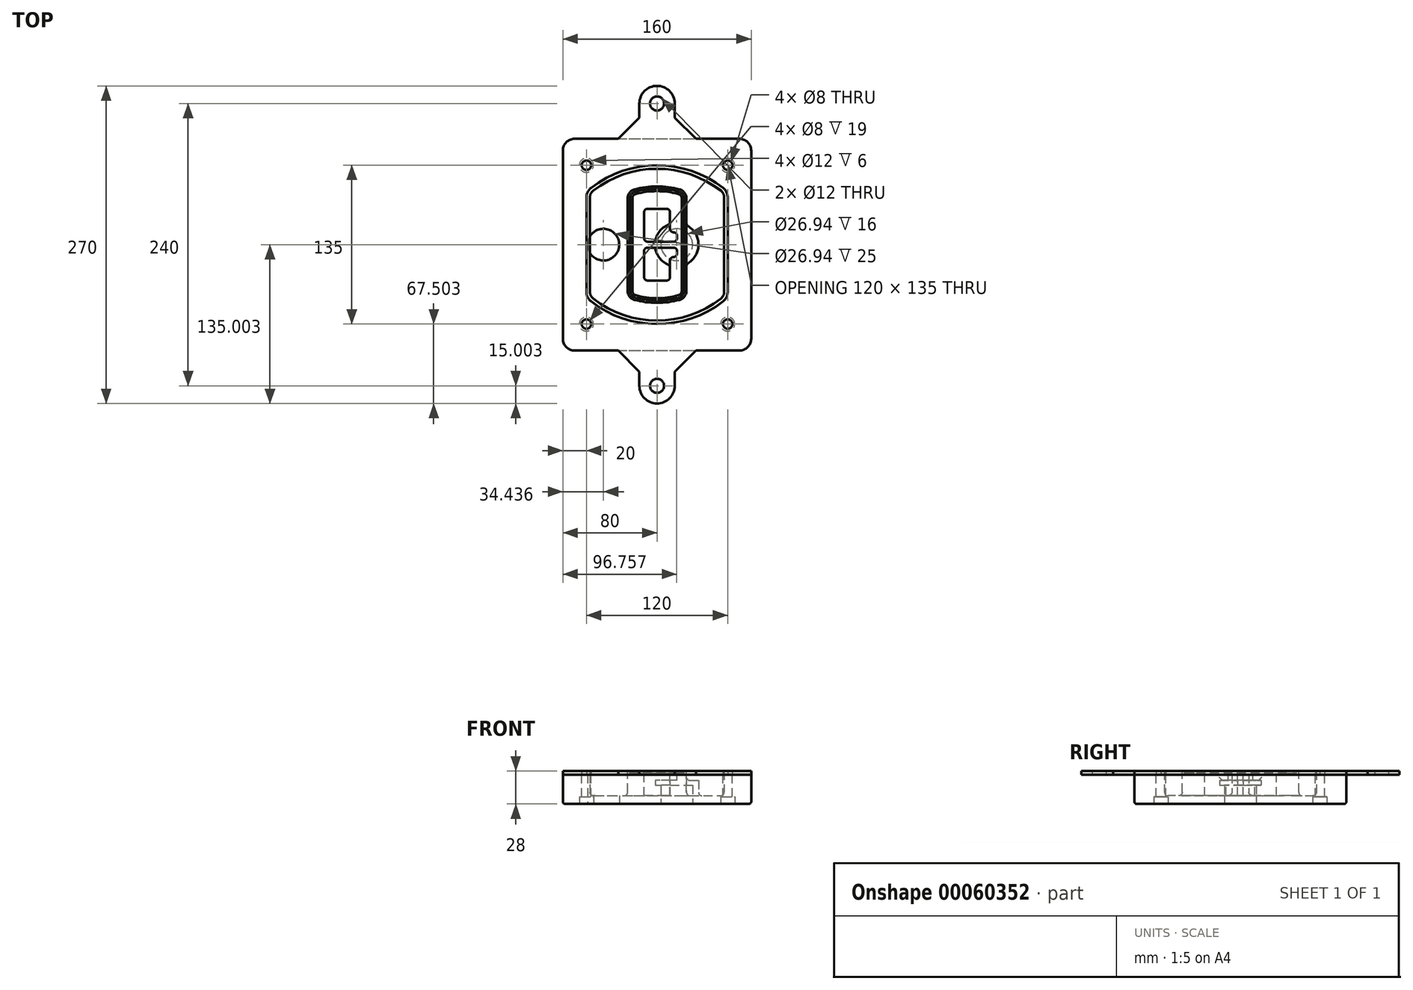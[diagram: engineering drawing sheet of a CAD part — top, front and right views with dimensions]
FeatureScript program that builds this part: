
annotation { "Feature Type Name" : "Feature", "Feature Type Description" : "" }
export const myFeature = defineFeature(function(context is Context, id is Id, definition is map)
    precondition{}
    {
        {
            var Q0;
            Q0=qCreatedBy(makeId("Top.planeOp"),FACE);
            var sketch = newSketch(context, id + "F0", { "sketchPlane" : qUnion([Q0])});
            skPoint(sketch, "E0.rect.middle", {"position": v(0, 0) * mm});
            skLineSegment(sketch, "E1.bottom", {"start": v(24.05, 28.38) * mm, "end": v(164.05, 28.38) * mm});
            skLineSegment(sketch, "E1.top", {"start": v(24.05, 208.38) * mm, "end": v(164.05, 208.38) * mm});
            skLineSegment(sketch, "E1.left", {"start": v(14.05, 38.38) * mm, "end": v(14.05, 198.38) * mm});
            skLineSegment(sketch, "E1.right", {"start": v(174.05, 38.38) * mm, "end": v(174.05, 198.38) * mm});
            skLineSegment(sketch, "E2", {"start": v(14.05, 208.38) * mm, "end": v(174.05, 28.38) * mm, "construction": true});
            skLineSegment(sketch, "E3", {"start": v(174.05, 208.38) * mm, "end": v(14.05, 28.38) * mm, "construction": true});
            skCircle(sketch, "E4", {"center": v(34.05, 185.88) * mm, "radius": 4 * mm});
            skCircle(sketch, "E5", {"center": v(154.05, 185.88) * mm, "radius": 4 * mm});
            skCircle(sketch, "E6", {"center": v(154.05, 50.88) * mm, "radius": 4 * mm});
            skCircle(sketch, "E7", {"center": v(34.05, 50.88) * mm, "radius": 4 * mm});
            skLineSegment(sketch, "E8", {"start": v(34.05, 185.88) * mm, "end": v(154.05, 185.88) * mm, "construction": true});
            skLineSegment(sketch, "E9", {"start": v(154.05, 185.88) * mm, "end": v(154.05, 50.88) * mm, "construction": true});
            skLineSegment(sketch, "E10", {"start": v(154.05, 50.88) * mm, "end": v(34.05, 50.88) * mm, "construction": true});
            skLineSegment(sketch, "E11", {"start": v(34.05, 50.88) * mm, "end": v(34.05, 185.88) * mm, "construction": true});
            skLineSegment(sketch, "E12", {"start": v(34.05, 158.68) * mm, "end": v(34.05, 78.09) * mm});
            skLineSegment(sketch, "E13", {"start": v(154.05, 158.68) * mm, "end": v(154.05, 78.09) * mm});
            skArc(sketch, "E14", {"start": v(150.2, 166.56) * mm, "mid": v(94.05, 185.88) * mm, "end": v(37.9, 166.56) * mm});
            skArc(sketch, "E15", {"start": v(37.9, 70.2) * mm, "mid": v(94.05, 50.88) * mm, "end": v(150.2, 70.2) * mm});
            skLineSegment(sketch, "E16", {"start": v(34.05, 118.38) * mm, "end": v(154.05, 118.38) * mm, "construction": true});
            skPoint(sketch, "E17.visualSharp", {"position": v(34.05, 73.38) * mm});
            skArc(sketch, "E17.filletArc", {"start": v(34.05, 78.09) * mm, "mid": v(35.06, 73.7) * mm, "end": v(37.9, 70.2) * mm});
            skPoint(sketch, "E18.visualSharp", {"position": v(34.05, 163.38) * mm});
            skArc(sketch, "E18.filletArc", {"start": v(37.9, 166.56) * mm, "mid": v(35.06, 163.06) * mm, "end": v(34.05, 158.68) * mm});
            skPoint(sketch, "E19.visualSharp", {"position": v(154.05, 163.38) * mm});
            skArc(sketch, "E19.filletArc", {"start": v(154.05, 158.68) * mm, "mid": v(153.04, 163.06) * mm, "end": v(150.2, 166.56) * mm});
            skPoint(sketch, "E20.visualSharp", {"position": v(154.05, 73.38) * mm});
            skArc(sketch, "E20.filletArc", {"start": v(150.2, 70.2) * mm, "mid": v(153.04, 73.7) * mm, "end": v(154.05, 78.09) * mm});
            skPoint(sketch, "E21.visualSharp", {"position": v(14.05, 208.38) * mm});
            skArc(sketch, "E21.filletArc", {"start": v(24.05, 208.38) * mm, "mid": v(16.98, 205.45) * mm, "end": v(14.05, 198.38) * mm});
            skPoint(sketch, "E22.visualSharp", {"position": v(174.05, 208.38) * mm});
            skArc(sketch, "E22.filletArc", {"start": v(174.05, 198.38) * mm, "mid": v(171.12, 205.45) * mm, "end": v(164.05, 208.38) * mm});
            skPoint(sketch, "E23.visualSharp", {"position": v(174.05, 28.38) * mm});
            skArc(sketch, "E23.filletArc", {"start": v(164.05, 28.38) * mm, "mid": v(171.12, 31.31) * mm, "end": v(174.05, 38.38) * mm});
            skPoint(sketch, "E24.visualSharp", {"position": v(14.05, 28.38) * mm});
            skArc(sketch, "E24.filletArc", {"start": v(14.05, 38.38) * mm, "mid": v(16.98, 31.31) * mm, "end": v(24.05, 28.38) * mm});
            skArc(sketch, "E25.0", {"start": v(151.05, 158.68) * mm, "mid": v(150.34, 161.75) * mm, "end": v(148.36, 164.2) * mm});
            skLineSegment(sketch, "E25.1", {"start": v(151.05, 158.68) * mm, "end": v(151.05, 78.09) * mm});
            skArc(sketch, "E25.2", {"start": v(148.36, 72.57) * mm, "mid": v(150.34, 75.02) * mm, "end": v(151.05, 78.09) * mm});
            skArc(sketch, "E25.3", {"start": v(39.74, 72.57) * mm, "mid": v(94.05, 53.88) * mm, "end": v(148.36, 72.57) * mm});
            skArc(sketch, "E25.4", {"start": v(37.05, 78.09) * mm, "mid": v(37.76, 75.02) * mm, "end": v(39.74, 72.57) * mm});
            skArc(sketch, "E25.5", {"start": v(148.36, 164.2) * mm, "mid": v(94.05, 182.88) * mm, "end": v(39.74, 164.2) * mm});
            skLineSegment(sketch, "E25.6", {"start": v(37.05, 158.68) * mm, "end": v(37.05, 78.09) * mm});
            skArc(sketch, "E25.7", {"start": v(39.74, 164.2) * mm, "mid": v(37.76, 161.75) * mm, "end": v(37.05, 158.68) * mm});
            skArc(sketch, "E26.0", {"start": v(35.43, 169.71) * mm, "mid": v(31.47, 164.82) * mm, "end": v(30.05, 158.68) * mm});
            skArc(sketch, "E26.1", {"start": v(152.67, 169.71) * mm, "mid": v(94.05, 189.88) * mm, "end": v(35.43, 169.71) * mm});
            skArc(sketch, "E26.2", {"start": v(158.05, 158.68) * mm, "mid": v(156.63, 164.82) * mm, "end": v(152.67, 169.71) * mm});
            skLineSegment(sketch, "E26.3", {"start": v(158.05, 158.68) * mm, "end": v(158.05, 78.09) * mm});
            skArc(sketch, "E26.4", {"start": v(152.67, 67.05) * mm, "mid": v(156.63, 71.95) * mm, "end": v(158.05, 78.09) * mm});
            skLineSegment(sketch, "E26.5", {"start": v(30.05, 158.68) * mm, "end": v(30.05, 78.09) * mm});
            skArc(sketch, "E26.6", {"start": v(35.43, 67.05) * mm, "mid": v(94.05, 46.88) * mm, "end": v(152.67, 67.05) * mm});
            skArc(sketch, "E26.7", {"start": v(30.05, 78.09) * mm, "mid": v(31.47, 71.95) * mm, "end": v(35.43, 67.05) * mm});
            skSolve(sketch);
        }
        {
            var Q0;
            Q0=makeQuery(id+"F0.imprint","IMPRINT",FACE,{"disambiguationData":[TD([[makeQuery(id+"F0.imprint","IMPRINT",EDGE,{"derivedFrom":sQuery(id+"F0.wireOp",EDGE,"E1.bottom")}),1.0]])]});
            var Q1;
            Q1=makeQuery(id+"F0.imprint","IMPRINT",FACE,{"disambiguationData":[TD([[makeQuery(id+"F0.imprint","IMPRINT",EDGE,{"derivedFrom":sQuery(id+"F0.wireOp",EDGE,"E12")}),1.0]])]});
            var Q2;
            Q2=makeQuery(id+"F0.imprint","IMPRINT",FACE,{"disambiguationData":[TD([[makeQuery(id+"F0.imprint","IMPRINT",EDGE,{"derivedFrom":sQuery(id+"F0.wireOp",EDGE,"E25.0")}),1.0]])]});
            var Q3;
            Q3=makeQuery(id+"F0.imprint","IMPRINT",FACE,{"disambiguationData":[TD([[makeQuery(id+"F0.imprint","IMPRINT",EDGE,{"derivedFrom":sQuery(id+"F0.wireOp",EDGE,"E12")}),-1.0]])]});
            extrude(context, id + "F1", {"entities" : qUnion([Q0, Q1, Q2, Q3]), "oppositeDirection" : true, "depth" : 25 * mm});
        }
        {
            var Q0;
            Q0=makeQuery(id+"F0.imprint","IMPRINT",FACE,{"disambiguationData":[TD([[makeQuery(id+"F0.imprint","IMPRINT",EDGE,{"derivedFrom":sQuery(id+"F0.wireOp",EDGE,"E12")}),1.0]])]});
            extrude(context, id + "F2", {"entities" : qUnion([Q0]), "operationType" : NewBodyOperationType.ADD, "depth" : 3 * mm});
        }
        {
            var Q0;
            Q0=makeQuery(id+"F0.imprint","IMPRINT",FACE,{"disambiguationData":[TD([[makeQuery(id+"F0.imprint","IMPRINT",EDGE,{"derivedFrom":sQuery(id+"F0.wireOp",EDGE,"E25.0")}),1.0]])]});
            extrude(context, id + "F3", {"entities" : qUnion([Q0]), "operationType" : NewBodyOperationType.REMOVE, "oppositeDirection" : true, "depth" : 18 * mm});
        }
        {
            var Q0;
            Q0=makeQuery(id+"F2.opExtrude","CAP_FACE",FACE,{"disambiguationData":[OSD([sQuery(id+"F0.wireOp",EDGE,"E12"),sQuery(id+"F0.wireOp",EDGE,"E13"),sQuery(id+"F0.wireOp",EDGE,"E14"),sQuery(id+"F0.wireOp",EDGE,"E15"),sQuery(id+"F0.wireOp",EDGE,"E17.filletArc"),sQuery(id+"F0.wireOp",EDGE,"E18.filletArc"),sQuery(id+"F0.wireOp",EDGE,"E19.filletArc"),sQuery(id+"F0.wireOp",EDGE,"E20.filletArc"),sQuery(id+"F0.wireOp",EDGE,"E25.0"),sQuery(id+"F0.wireOp",EDGE,"E25.1"),sQuery(id+"F0.wireOp",EDGE,"E25.2"),sQuery(id+"F0.wireOp",EDGE,"E25.3"),sQuery(id+"F0.wireOp",EDGE,"E25.4"),sQuery(id+"F0.wireOp",EDGE,"E25.5"),sQuery(id+"F0.wireOp",EDGE,"E25.6"),sQuery(id+"F0.wireOp",EDGE,"E25.7")])],"isStart":false});
            var sketch = newSketch(context, id + "F4", { "sketchPlane" : qUnion([Q0])});
            skArc(sketch, "E27.0", {"start": v(74.97, 71.41) * mm, "mid": v(94.05, 68.88) * mm, "end": v(113.13, 71.41) * mm});
            skArc(sketch, "E28.0", {"start": v(113.13, 165.35) * mm, "mid": v(94.05, 167.88) * mm, "end": v(74.97, 165.35) * mm});
            skLineSegment(sketch, "E29", {"start": v(69.05, 157.63) * mm, "end": v(69.05, 79.14) * mm});
            skLineSegment(sketch, "E30", {"start": v(119.05, 157.63) * mm, "end": v(119.05, 79.14) * mm});
            skLineSegment(sketch, "E31", {"start": v(69.05, 163.48) * mm, "end": v(119.05, 163.48) * mm, "construction": true});
            skLineSegment(sketch, "E32", {"start": v(69.05, 73.28) * mm, "end": v(119.05, 73.28) * mm, "construction": true});
            skPoint(sketch, "E33.visualSharp", {"position": v(69.05, 163.48) * mm});
            skArc(sketch, "E33.filletArc", {"start": v(74.97, 165.35) * mm, "mid": v(70.7, 162.5) * mm, "end": v(69.05, 157.63) * mm});
            skPoint(sketch, "E34.visualSharp", {"position": v(119.05, 163.48) * mm});
            skArc(sketch, "E34.filletArc", {"start": v(119.05, 157.63) * mm, "mid": v(117.4, 162.5) * mm, "end": v(113.13, 165.35) * mm});
            skPoint(sketch, "E35.visualSharp", {"position": v(119.05, 73.28) * mm});
            skArc(sketch, "E35.filletArc", {"start": v(113.13, 71.41) * mm, "mid": v(117.4, 74.27) * mm, "end": v(119.05, 79.14) * mm});
            skPoint(sketch, "E36.visualSharp", {"position": v(69.05, 73.28) * mm});
            skArc(sketch, "E36.filletArc", {"start": v(69.05, 79.14) * mm, "mid": v(70.7, 74.27) * mm, "end": v(74.97, 71.41) * mm});
            skArc(sketch, "E37.0", {"start": v(148.36, 164.2) * mm, "mid": v(94.05, 182.88) * mm, "end": v(39.74, 164.2) * mm});
            skArc(sketch, "E37.1", {"start": v(39.74, 164.2) * mm, "mid": v(37.76, 161.75) * mm, "end": v(37.05, 158.68) * mm});
            skLineSegment(sketch, "E37.2", {"start": v(37.05, 158.68) * mm, "end": v(37.05, 78.09) * mm});
            skArc(sketch, "E37.3", {"start": v(37.05, 78.09) * mm, "mid": v(37.76, 75.02) * mm, "end": v(39.74, 72.57) * mm});
            skArc(sketch, "E37.4", {"start": v(39.74, 72.57) * mm, "mid": v(94.05, 53.88) * mm, "end": v(148.36, 72.57) * mm});
            skArc(sketch, "E37.5", {"start": v(148.36, 72.57) * mm, "mid": v(150.34, 75.02) * mm, "end": v(151.05, 78.09) * mm});
            skLineSegment(sketch, "E37.6", {"start": v(151.05, 158.68) * mm, "end": v(151.05, 78.09) * mm});
            skArc(sketch, "E37.7", {"start": v(151.05, 158.68) * mm, "mid": v(150.34, 161.75) * mm, "end": v(148.36, 164.2) * mm});
            skLineSegment(sketch, "E38.0", {"start": v(117.05, 157.63) * mm, "end": v(117.05, 79.14) * mm});
            skArc(sketch, "E38.1", {"start": v(112.61, 73.34) * mm, "mid": v(115.81, 75.49) * mm, "end": v(117.05, 79.14) * mm});
            skArc(sketch, "E38.2", {"start": v(75.49, 73.34) * mm, "mid": v(94.05, 70.88) * mm, "end": v(112.61, 73.34) * mm});
            skArc(sketch, "E38.3", {"start": v(71.05, 79.14) * mm, "mid": v(72.29, 75.49) * mm, "end": v(75.49, 73.34) * mm});
            skLineSegment(sketch, "E38.4", {"start": v(71.05, 157.63) * mm, "end": v(71.05, 79.14) * mm});
            skArc(sketch, "E38.5", {"start": v(117.05, 157.63) * mm, "mid": v(115.81, 161.28) * mm, "end": v(112.61, 163.42) * mm});
            skArc(sketch, "E38.6", {"start": v(75.49, 163.42) * mm, "mid": v(72.29, 161.28) * mm, "end": v(71.05, 157.63) * mm});
            skArc(sketch, "E38.7", {"start": v(112.61, 163.42) * mm, "mid": v(94.05, 165.88) * mm, "end": v(75.49, 163.42) * mm});
            skArc(sketch, "E39.0", {"start": v(115.05, 157.63) * mm, "mid": v(114.23, 160.06) * mm, "end": v(112.1, 161.5) * mm});
            skLineSegment(sketch, "E39.1", {"start": v(115.05, 157.63) * mm, "end": v(115.05, 79.14) * mm});
            skArc(sketch, "E39.2", {"start": v(112.1, 75.27) * mm, "mid": v(114.23, 76.7) * mm, "end": v(115.05, 79.14) * mm});
            skArc(sketch, "E39.3", {"start": v(76, 75.27) * mm, "mid": v(94.05, 72.88) * mm, "end": v(112.1, 75.27) * mm});
            skArc(sketch, "E39.4", {"start": v(73.05, 79.14) * mm, "mid": v(73.87, 76.7) * mm, "end": v(76, 75.27) * mm});
            skArc(sketch, "E39.5", {"start": v(112.1, 161.5) * mm, "mid": v(94.05, 163.88) * mm, "end": v(76, 161.5) * mm});
            skLineSegment(sketch, "E39.6", {"start": v(73.05, 157.63) * mm, "end": v(73.05, 79.14) * mm});
            skArc(sketch, "E39.7", {"start": v(76, 161.5) * mm, "mid": v(73.87, 160.06) * mm, "end": v(73.05, 157.63) * mm});
            skLineSegment(sketch, "E40", {"start": v(69.05, 118.38) * mm, "end": v(119.05, 118.38) * mm, "construction": true});
            skLineSegment(sketch, "E41", {"start": v(83.05, 123.88) * mm, "end": v(83.05, 145.88) * mm});
            skLineSegment(sketch, "E42", {"start": v(86.05, 148.88) * mm, "end": v(102.05, 148.88) * mm});
            skLineSegment(sketch, "E43", {"start": v(105.05, 145.88) * mm, "end": v(105.05, 131.88) * mm});
            skLineSegment(sketch, "E44", {"start": v(108.05, 128.88) * mm, "end": v(108.05, 128.88) * mm});
            skLineSegment(sketch, "E45", {"start": v(111.05, 125.88) * mm, "end": v(111.05, 123.88) * mm});
            skLineSegment(sketch, "E46", {"start": v(108.05, 120.88) * mm, "end": v(86.05, 120.88) * mm});
            skPoint(sketch, "E47.visualSharp", {"position": v(83.05, 148.88) * mm});
            skArc(sketch, "E47.filletArc", {"start": v(86.05, 148.88) * mm, "mid": v(83.93, 148) * mm, "end": v(83.05, 145.88) * mm});
            skPoint(sketch, "E48.visualSharp", {"position": v(105.05, 148.88) * mm});
            skArc(sketch, "E48.filletArc", {"start": v(105.05, 145.88) * mm, "mid": v(104.17, 148) * mm, "end": v(102.05, 148.88) * mm});
            skPoint(sketch, "E49.visualSharp", {"position": v(105.05, 128.88) * mm});
            skArc(sketch, "E49.filletArc", {"start": v(105.05, 131.88) * mm, "mid": v(105.93, 129.76) * mm, "end": v(108.05, 128.88) * mm});
            skPoint(sketch, "E50.visualSharp", {"position": v(111.05, 128.88) * mm});
            skArc(sketch, "E50.filletArc", {"start": v(111.05, 125.88) * mm, "mid": v(110.17, 128) * mm, "end": v(108.05, 128.88) * mm});
            skPoint(sketch, "E51.visualSharp", {"position": v(111.05, 120.88) * mm});
            skArc(sketch, "E51.filletArc", {"start": v(108.05, 120.88) * mm, "mid": v(110.17, 121.76) * mm, "end": v(111.05, 123.88) * mm});
            skPoint(sketch, "E52.visualSharp", {"position": v(83.05, 120.88) * mm});
            skArc(sketch, "E52.filletArc", {"start": v(83.05, 123.88) * mm, "mid": v(83.93, 121.76) * mm, "end": v(86.05, 120.88) * mm});
            skLineSegment(sketch, "E53.0.MirrorCS", {"start": v(108.05, 115.88) * mm, "end": v(86.05, 115.88) * mm});
            skArc(sketch, "E54.0.MirrorCS", {"start": v(83.05, 112.88) * mm, "mid": v(83.93, 115) * mm, "end": v(86.05, 115.88) * mm});
            skLineSegment(sketch, "E55.0.MirrorCS", {"start": v(83.05, 112.88) * mm, "end": v(83.05, 90.88) * mm});
            skArc(sketch, "E56.0.MirrorCS", {"start": v(86.05, 87.88) * mm, "mid": v(83.93, 88.76) * mm, "end": v(83.05, 90.88) * mm});
            skLineSegment(sketch, "E57.0.MirrorCS", {"start": v(86.05, 87.88) * mm, "end": v(102.05, 87.88) * mm});
            skArc(sketch, "E58.0.MirrorCS", {"start": v(105.05, 90.88) * mm, "mid": v(104.17, 88.76) * mm, "end": v(102.05, 87.88) * mm});
            skLineSegment(sketch, "E59.0.MirrorCS", {"start": v(105.05, 90.88) * mm, "end": v(105.05, 104.88) * mm});
            skArc(sketch, "E60.0.MirrorCS", {"start": v(105.05, 104.88) * mm, "mid": v(105.93, 107) * mm, "end": v(108.05, 107.88) * mm});
            skArc(sketch, "E61.0.MirrorCS", {"start": v(111.05, 110.88) * mm, "mid": v(110.17, 108.76) * mm, "end": v(108.05, 107.88) * mm});
            skLineSegment(sketch, "E62.0.MirrorCS", {"start": v(111.05, 110.88) * mm, "end": v(111.05, 112.88) * mm});
            skArc(sketch, "E63.0.MirrorCS", {"start": v(108.05, 115.88) * mm, "mid": v(110.17, 115) * mm, "end": v(111.05, 112.88) * mm});
            skSolve(sketch);
        }
        {
            var Q0;
            Q0=makeQuery(id+"F4.imprint","IMPRINT",FACE,{"disambiguationData":[TD([[makeQuery(id+"F4.imprint","IMPRINT",EDGE,{"derivedFrom":sQuery(id+"F4.wireOp",EDGE,"E27.0")}),1.0]])]});
            var Q1;
            Q1=makeQuery(id+"F4.imprint","IMPRINT",FACE,{"disambiguationData":[TD([[makeQuery(id+"F4.imprint","IMPRINT",EDGE,{"derivedFrom":sQuery(id+"F4.wireOp",EDGE,"E38.0")}),-1.0]])]});
            var Q2;
            Q2=makeQuery(id+"F4.imprint","IMPRINT",FACE,{"disambiguationData":[TD([[makeQuery(id+"F4.imprint","IMPRINT",EDGE,{"derivedFrom":sQuery(id+"F4.wireOp",EDGE,"E39.0")}),1.0]])]});
            extrude(context, id + "F5", {"entities" : qUnion([Q0, Q1, Q2]), "operationType" : NewBodyOperationType.ADD, "endBound" : BoundingType.UP_TO_NEXT, "oppositeDirection" : true, "depth" : 25 * mm});
        }
        {
            var Q0;
            Q0=makeQuery(id+"F4.imprint","IMPRINT",FACE,{"disambiguationData":[TD([[makeQuery(id+"F4.imprint","IMPRINT",EDGE,{"derivedFrom":sQuery(id+"F4.wireOp",EDGE,"E38.0")}),-1.0]])]});
            extrude(context, id + "F6", {"entities" : qUnion([Q0]), "operationType" : NewBodyOperationType.REMOVE, "oppositeDirection" : true, "depth" : 2 * mm});
        }
        {
            var Q0;
            Q0=makeQuery(id+"F1.opExtrude","CAP_FACE",FACE,{"disambiguationData":[OSD([sQuery(id+"F0.wireOp",EDGE,"E1.bottom"),sQuery(id+"F0.wireOp",EDGE,"E1.top"),sQuery(id+"F0.wireOp",EDGE,"E1.left"),sQuery(id+"F0.wireOp",EDGE,"E1.right"),sQuery(id+"F0.wireOp",EDGE,"E4"),sQuery(id+"F0.wireOp",EDGE,"E5"),sQuery(id+"F0.wireOp",EDGE,"E6"),sQuery(id+"F0.wireOp",EDGE,"E7"),sQuery(id+"F0.wireOp",EDGE,"E21.filletArc"),sQuery(id+"F0.wireOp",EDGE,"E22.filletArc"),sQuery(id+"F0.wireOp",EDGE,"E23.filletArc"),sQuery(id+"F0.wireOp",EDGE,"E24.filletArc")])],"isStart":false});
            var sketch = newSketch(context, id + "F7", { "sketchPlane" : qUnion([Q0])});
            skCircle(sketch, "E64", {"center": v(110.8, -118.38) * mm, "radius": 13.47 * mm});
            skCircle(sketch, "E65", {"center": v(48.49, -118.38) * mm, "radius": 13.47 * mm});
            skLineSegment(sketch, "E66", {"start": v(174.05, -118.38) * mm, "end": v(14.05, -118.38) * mm});
            skCircle(sketch, "E67", {"center": v(110.8, -118.38) * mm, "radius": 18.47 * mm});
            skCircle(sketch, "E68", {"center": v(154.05, -185.88) * mm, "radius": 6 * mm});
            skCircle(sketch, "E69", {"center": v(34.05, -185.88) * mm, "radius": 6 * mm});
            skCircle(sketch, "E70", {"center": v(34.05, -50.88) * mm, "radius": 6 * mm});
            skCircle(sketch, "E71", {"center": v(154.05, -50.88) * mm, "radius": 6 * mm});
            skSolve(sketch);
        }
        {
            var Q0;
            {var subQ1=sQuery(id+"F7.wireOp",EDGE,"E66");var subQ4=sQuery(id+"F7.wireOp",EDGE,"E64");var subQ6=makeQuery(id+"F7.imprint","INTERSECT",VERTEX,{"disambiguationData":[OD(0.0)],"derivedFrom":[subQ4,subQ1]});Q0=makeQuery(id+"F7.imprint","IMPRINT",FACE,{"disambiguationData":[TD([[makeQuery(id+"F7.imprint","IMPRINT",EDGE,{"disambiguationData":[TD([[subQ6,-1.0]])],"derivedFrom":subQ4}),-1.0]])]});}
            var Q1;
            {var subQ0=sQuery(id+"F7.wireOp",EDGE,"E66");var subQ1=sQuery(id+"F7.wireOp",EDGE,"E64");var subQ3=makeQuery(id+"F7.imprint","INTERSECT",VERTEX,{"disambiguationData":[OD(0.0)],"derivedFrom":[subQ1,subQ0]});Q1=makeQuery(id+"F7.imprint","IMPRINT",FACE,{"disambiguationData":[TD([[makeQuery(id+"F7.imprint","IMPRINT",EDGE,{"disambiguationData":[TD([[subQ3,-1.0]])],"derivedFrom":subQ1}),1.0]])]});}
            var Q2;
            {var subQ0=sQuery(id+"F7.wireOp",EDGE,"E66");var subQ1=sQuery(id+"F7.wireOp",EDGE,"E64");var subQ3=makeQuery(id+"F7.imprint","INTERSECT",VERTEX,{"disambiguationData":[OD(0.0)],"derivedFrom":[subQ1,subQ0]});Q2=makeQuery(id+"F7.imprint","IMPRINT",FACE,{"disambiguationData":[TD([[makeQuery(id+"F7.imprint","IMPRINT",EDGE,{"disambiguationData":[TD([[subQ3,1.0]])],"derivedFrom":subQ1}),1.0]])]});}
            var Q3;
            {var subQ1=sQuery(id+"F7.wireOp",EDGE,"E66");var subQ4=sQuery(id+"F7.wireOp",EDGE,"E64");var subQ6=makeQuery(id+"F7.imprint","INTERSECT",VERTEX,{"disambiguationData":[OD(0.0)],"derivedFrom":[subQ4,subQ1]});Q3=makeQuery(id+"F7.imprint","IMPRINT",FACE,{"disambiguationData":[TD([[makeQuery(id+"F7.imprint","IMPRINT",EDGE,{"disambiguationData":[TD([[subQ6,1.0]])],"derivedFrom":subQ4}),-1.0]])]});}
            extrude(context, id + "F8", {"entities" : qUnion([Q0, Q1, Q2, Q3]), "operationType" : NewBodyOperationType.ADD, "oppositeDirection" : true, "depth" : 20 * mm});
        }
        {
            var Q0;
            {var subQ0=sQuery(id+"F7.wireOp",EDGE,"E66");var subQ1=sQuery(id+"F7.wireOp",EDGE,"E64");var subQ3=makeQuery(id+"F7.imprint","INTERSECT",VERTEX,{"disambiguationData":[OD(0.0)],"derivedFrom":[subQ1,subQ0]});Q0=makeQuery(id+"F7.imprint","IMPRINT",FACE,{"disambiguationData":[TD([[makeQuery(id+"F7.imprint","IMPRINT",EDGE,{"disambiguationData":[TD([[subQ3,-1.0]])],"derivedFrom":subQ1}),1.0]])]});}
            var Q1;
            {var subQ0=sQuery(id+"F7.wireOp",EDGE,"E66");var subQ1=sQuery(id+"F7.wireOp",EDGE,"E64");var subQ3=makeQuery(id+"F7.imprint","INTERSECT",VERTEX,{"disambiguationData":[OD(0.0)],"derivedFrom":[subQ1,subQ0]});Q1=makeQuery(id+"F7.imprint","IMPRINT",FACE,{"disambiguationData":[TD([[makeQuery(id+"F7.imprint","IMPRINT",EDGE,{"disambiguationData":[TD([[subQ3,1.0]])],"derivedFrom":subQ1}),1.0]])]});}
            extrude(context, id + "F9", {"entities" : qUnion([Q0, Q1]), "operationType" : NewBodyOperationType.REMOVE, "oppositeDirection" : true, "depth" : 16 * mm});
        }
        {
            var Q0;
            {var subQ0=sQuery(id+"F7.wireOp",EDGE,"E66");var subQ1=sQuery(id+"F7.wireOp",EDGE,"E65");var subQ3=makeQuery(id+"F7.imprint","INTERSECT",VERTEX,{"disambiguationData":[OD(0.0)],"derivedFrom":[subQ1,subQ0]});Q0=makeQuery(id+"F7.imprint","IMPRINT",FACE,{"disambiguationData":[TD([[makeQuery(id+"F7.imprint","IMPRINT",EDGE,{"disambiguationData":[TD([[subQ3,-1.0]])],"derivedFrom":subQ1}),1.0]])]});}
            var Q1;
            {var subQ0=sQuery(id+"F7.wireOp",EDGE,"E66");var subQ1=sQuery(id+"F7.wireOp",EDGE,"E65");var subQ3=makeQuery(id+"F7.imprint","INTERSECT",VERTEX,{"disambiguationData":[OD(0.0)],"derivedFrom":[subQ1,subQ0]});Q1=makeQuery(id+"F7.imprint","IMPRINT",FACE,{"disambiguationData":[TD([[makeQuery(id+"F7.imprint","IMPRINT",EDGE,{"disambiguationData":[TD([[subQ3,1.0]])],"derivedFrom":subQ1}),1.0]])]});}
            extrude(context, id + "F10", {"entities" : qUnion([Q0, Q1]), "operationType" : NewBodyOperationType.REMOVE, "oppositeDirection" : true, "depth" : 25 * mm});
        }
        {
            var Q0;
            Q0=makeQuery(id+"F7.imprint","IMPRINT",FACE,{"disambiguationData":[TD([[makeQuery(id+"F7.imprint","IMPRINT",EDGE,{"derivedFrom":sQuery(id+"F7.wireOp",EDGE,"E68")}),1.0]])]});
            var Q1;
            Q1=makeQuery(id+"F7.imprint","IMPRINT",FACE,{"disambiguationData":[TD([[makeQuery(id+"F7.imprint","IMPRINT",EDGE,{"derivedFrom":makeQuery(id+"F1.opExtrude","CAP_EDGE",EDGE,{"disambiguationData":[OSD([sQuery(id+"F0.wireOp",EDGE,"E5")])],"isStart":false})}),-1.0]])]});
            var Q2;
            Q2=makeQuery(id+"F7.imprint","IMPRINT",FACE,{"disambiguationData":[TD([[makeQuery(id+"F7.imprint","IMPRINT",EDGE,{"derivedFrom":sQuery(id+"F7.wireOp",EDGE,"E69")}),1.0]])]});
            var Q3;
            Q3=makeQuery(id+"F7.imprint","IMPRINT",FACE,{"disambiguationData":[TD([[makeQuery(id+"F7.imprint","IMPRINT",EDGE,{"derivedFrom":makeQuery(id+"F1.opExtrude","CAP_EDGE",EDGE,{"disambiguationData":[OSD([sQuery(id+"F0.wireOp",EDGE,"E4")])],"isStart":false})}),-1.0]])]});
            var Q4;
            Q4=makeQuery(id+"F7.imprint","IMPRINT",FACE,{"disambiguationData":[TD([[makeQuery(id+"F7.imprint","IMPRINT",EDGE,{"derivedFrom":sQuery(id+"F7.wireOp",EDGE,"E70")}),1.0]])]});
            var Q5;
            Q5=makeQuery(id+"F7.imprint","IMPRINT",FACE,{"disambiguationData":[TD([[makeQuery(id+"F7.imprint","IMPRINT",EDGE,{"derivedFrom":makeQuery(id+"F1.opExtrude","CAP_EDGE",EDGE,{"disambiguationData":[OSD([sQuery(id+"F0.wireOp",EDGE,"E7")])],"isStart":false})}),-1.0]])]});
            var Q6;
            Q6=makeQuery(id+"F7.imprint","IMPRINT",FACE,{"disambiguationData":[TD([[makeQuery(id+"F7.imprint","IMPRINT",EDGE,{"derivedFrom":sQuery(id+"F7.wireOp",EDGE,"E71")}),1.0]])]});
            var Q7;
            Q7=makeQuery(id+"F7.imprint","IMPRINT",FACE,{"disambiguationData":[TD([[makeQuery(id+"F7.imprint","IMPRINT",EDGE,{"derivedFrom":makeQuery(id+"F1.opExtrude","CAP_EDGE",EDGE,{"disambiguationData":[OSD([sQuery(id+"F0.wireOp",EDGE,"E6")])],"isStart":false})}),-1.0]])]});
            extrude(context, id + "F11", {"entities" : qUnion([Q0, Q1, Q2, Q3, Q4, Q5, Q6, Q7]), "operationType" : NewBodyOperationType.REMOVE, "oppositeDirection" : true, "depth" : 6 * mm});
        }
        {
            var Q0;
            Q0=makeQuery(id+"F9.boolean.opBoolean","COPY",FACE,{"derivedFrom":makeQuery(id+"F9.opExtrude","CAP_FACE",FACE,{"disambiguationData":[OSD([sQuery(id+"F7.wireOp",EDGE,"E64")])],"isStart":false})});
            var sketch = newSketch(context, id + "F12", { "sketchPlane" : qUnion([Q0])});
            skArc(sketch, "E72.0", {"start": v(105.05, -100.83) * mm, "mid": v(96.62, -106.56) * mm, "end": v(92.5, -115.88) * mm});
            skArc(sketch, "E72.1", {"start": v(92.5, -120.88) * mm, "mid": v(96.62, -130.2) * mm, "end": v(105.05, -135.93) * mm});
            skLineSegment(sketch, "E73", {"start": v(92.5, -120.88) * mm, "end": v(108.05, -120.88) * mm});
            skLineSegment(sketch, "E74.0", {"start": v(108.05, -115.88) * mm, "end": v(92.5, -115.88) * mm});
            skArc(sketch, "E74.1", {"start": v(108.05, -115.88) * mm, "mid": v(110.17, -115) * mm, "end": v(111.05, -112.88) * mm});
            skLineSegment(sketch, "E74.2", {"start": v(111.05, -110.88) * mm, "end": v(111.05, -112.88) * mm});
            skArc(sketch, "E74.3", {"start": v(111.05, -110.88) * mm, "mid": v(110.17, -108.76) * mm, "end": v(108.05, -107.88) * mm});
            skArc(sketch, "E74.4", {"start": v(105.05, -104.88) * mm, "mid": v(105.93, -107) * mm, "end": v(108.05, -107.88) * mm});
            skLineSegment(sketch, "E74.5", {"start": v(105.05, -100.83) * mm, "end": v(105.05, -104.88) * mm});
            skLineSegment(sketch, "E74.7", {"start": v(108.05, -120.88) * mm, "end": v(92.5, -120.88) * mm});
            skArc(sketch, "E74.8", {"start": v(108.05, -120.88) * mm, "mid": v(110.17, -121.76) * mm, "end": v(111.05, -123.88) * mm});
            skLineSegment(sketch, "E74.9", {"start": v(111.05, -125.88) * mm, "end": v(111.05, -123.88) * mm});
            skArc(sketch, "E74.10", {"start": v(111.05, -125.88) * mm, "mid": v(110.17, -128) * mm, "end": v(108.05, -128.88) * mm});
            skArc(sketch, "E74.11", {"start": v(105.05, -131.88) * mm, "mid": v(105.93, -129.76) * mm, "end": v(108.05, -128.88) * mm});
            skLineSegment(sketch, "E74.12", {"start": v(105.05, -135.93) * mm, "end": v(105.05, -131.88) * mm});
            skPoint(sketch, "E75.orphan", {"position": v(105.05, -145.88) * mm});
            skPoint(sketch, "E76.orphan", {"position": v(86.05, -120.88) * mm});
            skPoint(sketch, "E77.orphan", {"position": v(86.05, -115.88) * mm});
            skPoint(sketch, "E78.orphan", {"position": v(105.05, -90.88) * mm});
            skSolve(sketch);
        }
        {
            var Q0;
            {var subQ7=sQuery(id+"F12.wireOp",EDGE,"E72.0");var subQ14=sQuery(id+"F12.wireOp",EDGE,"E72.1");var subQ16=sQuery(id+"F12.wireOp",EDGE,"E74.1");var subQ18=sQuery(id+"F12.wireOp",EDGE,"E74.8");Q0=qUnion([makeQuery(id+"F12.imprint","IMPRINT",FACE,{"disambiguationData":[TD([[makeQuery(id+"F12.imprint","IMPRINT",EDGE,{"derivedFrom":subQ7}),1.0]])]}),makeQuery(id+"F12.imprint","IMPRINT",FACE,{"disambiguationData":[TD([[makeQuery(id+"F12.imprint","IMPRINT",EDGE,{"derivedFrom":subQ14}),1.0]])]}),makeQuery(id+"F12.imprint","IMPRINT",FACE,{"disambiguationData":[TD([[makeQuery(id+"F12.imprint","IMPRINT",EDGE,{"derivedFrom":subQ16}),1.0]])]}),makeQuery(id+"F12.imprint","IMPRINT",FACE,{"disambiguationData":[TD([[makeQuery(id+"F12.imprint","IMPRINT",EDGE,{"derivedFrom":subQ18}),-1.0]])]})]);}
            var Q1;
            Q1=makeQuery(id+"F5.boolean.opBoolean","SPLIT",FACE,{"disambiguationData":[TD([makeQuery(id+"F5.opExtrude","SWEPT_FACE",FACE,{"disambiguationData":[OSD([sQuery(id+"F4.wireOp",EDGE,"E41")])]})])],"derivedFrom":makeQuery(id+"F3.boolean.opBoolean","COPY",FACE,{"derivedFrom":makeQuery(id+"F3.opExtrude","CAP_FACE",FACE,{"disambiguationData":[OSD([sQuery(id+"F0.wireOp",EDGE,"E25.0"),sQuery(id+"F0.wireOp",EDGE,"E25.1"),sQuery(id+"F0.wireOp",EDGE,"E25.2"),sQuery(id+"F0.wireOp",EDGE,"E25.3"),sQuery(id+"F0.wireOp",EDGE,"E25.4"),sQuery(id+"F0.wireOp",EDGE,"E25.5"),sQuery(id+"F0.wireOp",EDGE,"E25.6"),sQuery(id+"F0.wireOp",EDGE,"E25.7")])],"isStart":false})})});
            extrude(context, id + "F13", {"entities" : qUnion([Q0]), "operationType" : NewBodyOperationType.REMOVE, "endBound" : BoundingType.UP_TO_SURFACE, "endBoundEntityFace" : qUnion([Q1]), "depth" : 25 * mm});
        }
        {
            var Q0;
            Q0=makeQuery(id+"F3.boolean.opBoolean","COPY",EDGE,{"derivedFrom":makeQuery(id+"F3.opExtrude","CAP_EDGE",EDGE,{"disambiguationData":[OSD([sQuery(id+"F0.wireOp",EDGE,"E25.6")])],"isStart":false})});
            var Q1;
            Q1=makeQuery(id+"F8.boolean.opBoolean","INTERSECT",EDGE,{"derivedFrom":[makeQuery(id+"F5.opExtrude","SWEPT_FACE",FACE,{"disambiguationData":[OSD([sQuery(id+"F4.wireOp",EDGE,"E30")])]}),makeQuery(id+"F8.opExtrude","CAP_FACE",FACE,{"disambiguationData":[OSD([sQuery(id+"F7.wireOp",EDGE,"E67")])],"isStart":false})]});
            var Q2;
            Q2=makeQuery(id+"F8.boolean.opBoolean","INTERSECT",EDGE,{"disambiguationData":[OD(1.0)],"derivedFrom":[makeQuery(id+"F5.opExtrude","SWEPT_FACE",FACE,{"disambiguationData":[OSD([sQuery(id+"F4.wireOp",EDGE,"E30")])]}),makeQuery(id+"F8.opExtrude","SWEPT_FACE",FACE,{"disambiguationData":[OSD([sQuery(id+"F7.wireOp",EDGE,"E67")])]})]});
            var Q3;
            {var subQ0=sQuery(id+"F4.wireOp",EDGE,"E30");Q3=makeQuery(id+"F8.boolean.opBoolean","SPLIT",EDGE,{"disambiguationData":[TD([makeQuery(id+"F5.opExtrude","SWEPT_FACE",FACE,{"disambiguationData":[OSD([sQuery(id+"F4.wireOp",EDGE,"E35.filletArc")])]})])],"derivedFrom":makeQuery(id+"F5.opExtrude","CAP_EDGE",EDGE,{"disambiguationData":[OSD([subQ0])],"isStart":false})});}
            var Q4;
            {var subQ0=sQuery(id+"F0.wireOp",EDGE,"E25.7");var subQ1=sQuery(id+"F0.wireOp",EDGE,"E25.1");var subQ2=sQuery(id+"F0.wireOp",EDGE,"E25.6");var subQ3=sQuery(id+"F0.wireOp",EDGE,"E25.5");var subQ4=sQuery(id+"F0.wireOp",EDGE,"E25.4");var subQ5=sQuery(id+"F0.wireOp",EDGE,"E25.0");var subQ6=sQuery(id+"F0.wireOp",EDGE,"E25.2");var subQ7=sQuery(id+"F0.wireOp",EDGE,"E25.3");Q4=makeQuery(id+"F8.boolean.opBoolean","INTERSECT",EDGE,{"derivedFrom":[makeQuery(id+"F5.boolean.opBoolean","SPLIT",FACE,{"disambiguationData":[TD([makeQuery(id+"F2.opExtrude","SWEPT_FACE",FACE,{"disambiguationData":[OSD([subQ5])]})])],"derivedFrom":makeQuery(id+"F3.boolean.opBoolean","COPY",FACE,{"derivedFrom":makeQuery(id+"F3.opExtrude","CAP_FACE",FACE,{"disambiguationData":[OSD([subQ5,subQ1,subQ6,subQ7,subQ4,subQ3,subQ2,subQ0])],"isStart":false})})}),makeQuery(id+"F8.opExtrude","SWEPT_FACE",FACE,{"disambiguationData":[OSD([sQuery(id+"F7.wireOp",EDGE,"E67")])]})]});}
            var Q5;
            Q5=makeQuery(id+"F8.boolean.opBoolean","INTERSECT",EDGE,{"disambiguationData":[OD(0.0)],"derivedFrom":[makeQuery(id+"F5.opExtrude","SWEPT_FACE",FACE,{"disambiguationData":[OSD([sQuery(id+"F4.wireOp",EDGE,"E30")])]}),makeQuery(id+"F8.opExtrude","SWEPT_FACE",FACE,{"disambiguationData":[OSD([sQuery(id+"F7.wireOp",EDGE,"E67")])]})]});
            fillet(context, id + "F14", {"entities" : qUnion([Q0, Q1, Q2, Q3, Q4, Q5]), "radius" : 3 * mm, "tangentPropagation" : true, "allowEdgeOverflow" : false});
        }
        {
            var Q0;
            Q0=makeQuery(id+"F1.opExtrude","CAP_EDGE",EDGE,{"disambiguationData":[OSD([sQuery(id+"F0.wireOp",EDGE,"E1.bottom")])],"isStart":false});
            fillet(context, id + "F15", {"entities" : qUnion([Q0]), "radius" : 2 * mm, "tangentPropagation" : true, "allowEdgeOverflow" : false});
        }
        {
            var Q0;
            {var subQ0=sQuery(id+"F0.wireOp",EDGE,"E22.filletArc");var subQ1=sQuery(id+"F0.wireOp",EDGE,"E7");var subQ2=sQuery(id+"F0.wireOp",EDGE,"E6");var subQ3=sQuery(id+"F0.wireOp",EDGE,"E5");var subQ4=sQuery(id+"F0.wireOp",EDGE,"E4");var subQ5=sQuery(id+"F0.wireOp",EDGE,"E1.bottom");var subQ6=sQuery(id+"F0.wireOp",EDGE,"E21.filletArc");var subQ7=sQuery(id+"F0.wireOp",EDGE,"E1.top");var subQ8=sQuery(id+"F0.wireOp",EDGE,"E1.left");var subQ9=sQuery(id+"F0.wireOp",EDGE,"E1.right");var subQ10=sQuery(id+"F0.wireOp",EDGE,"E23.filletArc");var subQ11=sQuery(id+"F0.wireOp",EDGE,"E24.filletArc");Q0=makeQuery(id+"F2.boolean.opBoolean","SPLIT",FACE,{"disambiguationData":[TD([makeQuery(id+"F1.opExtrude","SWEPT_FACE",FACE,{"disambiguationData":[OSD([subQ5])]})])],"derivedFrom":makeQuery(id+"F1.opExtrude","CAP_FACE",FACE,{"disambiguationData":[OSD([subQ5,subQ7,subQ8,subQ9,subQ4,subQ3,subQ2,subQ1,subQ6,subQ0,subQ10,subQ11])],"isStart":true})});}
            var sketch = newSketch(context, id + "F16", { "sketchPlane" : qUnion([Q0])});
            skLineSegment(sketch, "E79", {"start": v(94.05, 208.38) * mm, "end": v(94.05, 238.38) * mm, "construction": true});
            skCircle(sketch, "E80", {"center": v(94.05, 238.38) * mm, "radius": 6 * mm});
            skLineSegment(sketch, "E81", {"start": v(79.05, 238.38) * mm, "end": v(79.05, 226.38) * mm});
            skLineSegment(sketch, "E82", {"start": v(79.05, 226.38) * mm, "end": v(61.05, 208.38) * mm});
            skLineSegment(sketch, "E83", {"start": v(109.05, 238.38) * mm, "end": v(109.05, 226.38) * mm});
            skArc(sketch, "E84", {"start": v(109.05, 238.38) * mm, "mid": v(94.05, 253.38) * mm, "end": v(79.05, 238.38) * mm});
            skLineSegment(sketch, "E85", {"start": v(109.05, 226.38) * mm, "end": v(127.05, 208.38) * mm});
            skLineSegment(sketch, "E86", {"start": v(14.05, 118.38) * mm, "end": v(174.05, 118.38) * mm, "construction": true});
            skLineSegment(sketch, "E87.MirrorCS", {"start": v(109.05, -1.62) * mm, "end": v(109.05, 10.38) * mm});
            skLineSegment(sketch, "E88.MirrorCS", {"start": v(79.05, -1.62) * mm, "end": v(79.05, 10.38) * mm});
            skLineSegment(sketch, "E89.MirrorCS", {"start": v(79.05, 10.38) * mm, "end": v(61.05, 28.38) * mm});
            skArc(sketch, "E90.MirrorCS", {"start": v(109.05, -1.62) * mm, "mid": v(94.05, -16.62) * mm, "end": v(79.05, -1.62) * mm});
            skCircle(sketch, "E91.MirrorC", {"center": v(94.05, -1.62) * mm, "radius": 6 * mm});
            skLineSegment(sketch, "E92.MirrorCS", {"start": v(94.05, 28.38) * mm, "end": v(94.05, -1.62) * mm, "construction": true});
            skLineSegment(sketch, "E93.MirrorCS", {"start": v(109.05, 10.38) * mm, "end": v(127.05, 28.38) * mm});
            skSolve(sketch);
        }
        {
            var Q0;
            Q0=makeQuery(id+"F16.imprint","IMPRINT",FACE,{"disambiguationData":[TD([[makeQuery(id+"F16.imprint","IMPRINT",EDGE,{"derivedFrom":sQuery(id+"F16.wireOp",EDGE,"E80")}),-1.0]])]});
            var Q1;
            Q1=makeQuery(id+"F16.imprint","IMPRINT",FACE,{"disambiguationData":[TD([[makeQuery(id+"F16.imprint","IMPRINT",EDGE,{"derivedFrom":makeQuery(id+"F1.opExtrude","CAP_EDGE",EDGE,{"disambiguationData":[OSD([sQuery(id+"F0.wireOp",EDGE,"E1.left")])],"isStart":true})}),-1.0]])]});
            var Q2;
            Q2=makeQuery(id+"F16.imprint","IMPRINT",FACE,{"disambiguationData":[TD([[makeQuery(id+"F16.imprint","IMPRINT",EDGE,{"derivedFrom":sQuery(id+"F16.wireOp",EDGE,"E87.MirrorCS")}),1.0]])]});
            var Q3;
            {var subQ0=sQuery(id+"F4.wireOp",EDGE,"E63.0.MirrorCS");var subQ1=sQuery(id+"F4.wireOp",EDGE,"E62.0.MirrorCS");var subQ2=sQuery(id+"F4.wireOp",EDGE,"E61.0.MirrorCS");var subQ3=sQuery(id+"F4.wireOp",EDGE,"E60.0.MirrorCS");var subQ4=sQuery(id+"F4.wireOp",EDGE,"E59.0.MirrorCS");var subQ5=sQuery(id+"F4.wireOp",EDGE,"E58.0.MirrorCS");var subQ6=sQuery(id+"F4.wireOp",EDGE,"E57.0.MirrorCS");var subQ7=sQuery(id+"F4.wireOp",EDGE,"E56.0.MirrorCS");var subQ8=sQuery(id+"F4.wireOp",EDGE,"E55.0.MirrorCS");var subQ9=sQuery(id+"F4.wireOp",EDGE,"E54.0.MirrorCS");var subQ10=sQuery(id+"F4.wireOp",EDGE,"E53.0.MirrorCS");var subQ11=sQuery(id+"F4.wireOp",EDGE,"E52.filletArc");var subQ12=sQuery(id+"F4.wireOp",EDGE,"E45");var subQ13=sQuery(id+"F4.wireOp",EDGE,"E43");var subQ14=sQuery(id+"F4.wireOp",EDGE,"E42");var subQ15=sQuery(id+"F4.wireOp",EDGE,"E41");var subQ16=sQuery(id+"F4.wireOp",EDGE,"E46");var subQ17=sQuery(id+"F4.wireOp",EDGE,"E47.filletArc");var subQ18=sQuery(id+"F4.wireOp",EDGE,"E48.filletArc");var subQ19=sQuery(id+"F4.wireOp",EDGE,"E49.filletArc");var subQ20=sQuery(id+"F4.wireOp",EDGE,"E50.filletArc");var subQ21=sQuery(id+"F4.wireOp",EDGE,"E51.filletArc");Q3=makeQuery(id+"F6.boolean.opBoolean","SPLIT",FACE,{"disambiguationData":[TD([makeQuery(id+"F5.opExtrude","SWEPT_FACE",FACE,{"disambiguationData":[OSD([subQ15])]})])],"derivedFrom":makeQuery(id+"F5.opExtrude","CAP_FACE",FACE,{"disambiguationData":[OSD([sQuery(id+"F4.wireOp",EDGE,"E27.0"),sQuery(id+"F4.wireOp",EDGE,"E28.0"),sQuery(id+"F4.wireOp",EDGE,"E29"),sQuery(id+"F4.wireOp",EDGE,"E30"),sQuery(id+"F4.wireOp",EDGE,"E33.filletArc"),sQuery(id+"F4.wireOp",EDGE,"E34.filletArc"),sQuery(id+"F4.wireOp",EDGE,"E35.filletArc"),sQuery(id+"F4.wireOp",EDGE,"E36.filletArc"),subQ15,subQ14,subQ13,subQ12,subQ16,subQ17,subQ18,subQ19,subQ20,subQ21,subQ11,subQ10,subQ9,subQ8,subQ7,subQ6,subQ5,subQ4,subQ3,subQ2,subQ1,subQ0])],"isStart":true})});}
            extrude(context, id + "F17", {"entities" : qUnion([Q0, Q1, Q2]), "endBound" : BoundingType.UP_TO_SURFACE, "endBoundEntityFace" : qUnion([Q3]), "depth" : 25 * mm});
        }
    });
